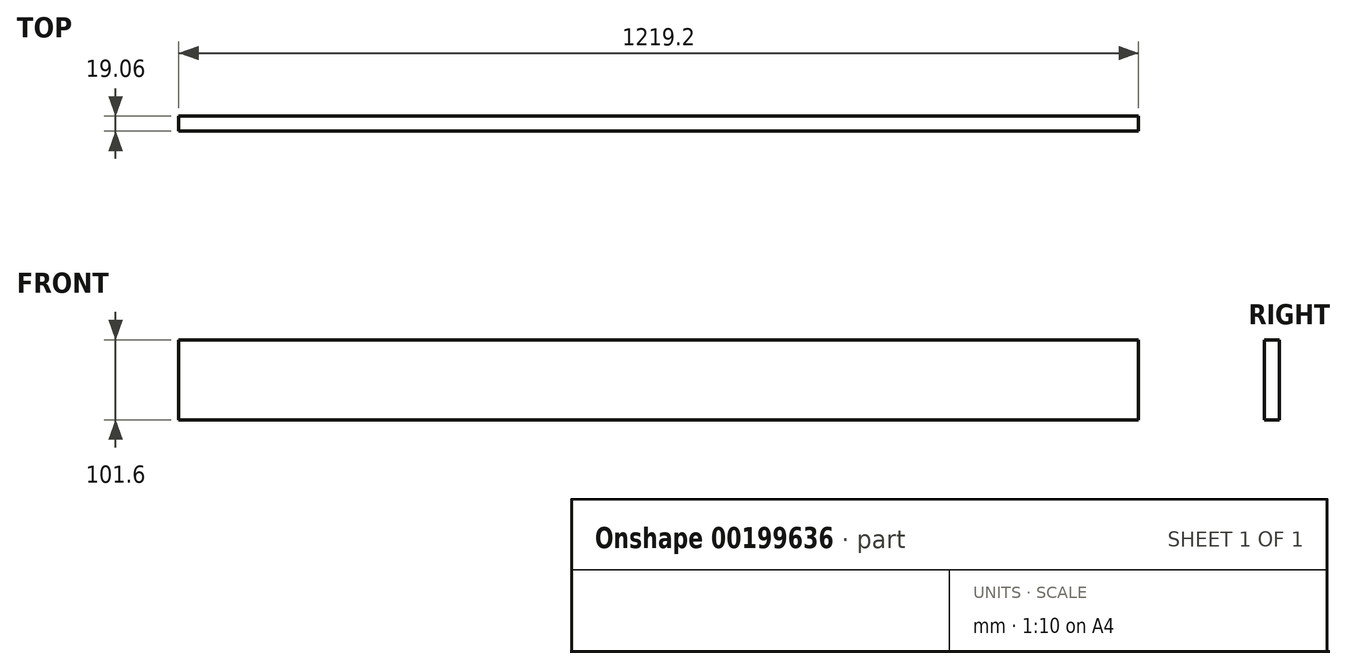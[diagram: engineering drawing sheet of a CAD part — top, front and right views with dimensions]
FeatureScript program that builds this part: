
annotation { "Feature Type Name" : "Feature", "Feature Type Description" : "" }
export const myFeature = defineFeature(function(context is Context, id is Id, definition is map)
    precondition{}
    {
        {
            var Q0;
            Q0=qCreatedBy(makeId("Front.planeOp"),FACE);
            var sketch = newSketch(context, id + "F0", { "sketchPlane" : qUnion([Q0])});
            skLineSegment(sketch, "E0.bottom", {"start": v(-557.63, 26.65) * mm, "end": v(661.57, 26.65) * mm});
            skLineSegment(sketch, "E0.top", {"start": v(-557.63, -74.95) * mm, "end": v(661.57, -74.95) * mm});
            skLineSegment(sketch, "E0.left", {"start": v(-557.63, 26.65) * mm, "end": v(-557.63, -74.95) * mm});
            skLineSegment(sketch, "E0.right", {"start": v(661.57, 26.65) * mm, "end": v(661.57, -74.95) * mm});
            skSolve(sketch);
        }
        {
            var Q0;
            Q0=makeQuery(id+"F0.imprint","IMPRINT",FACE,{"disambiguationData":[TD([[makeQuery(id+"F0.imprint","IMPRINT",EDGE,{"derivedFrom":sQuery(id+"F0.wireOp",EDGE,"E0.bottom")}),-1.0]])]});
            extrude(context, id + "F1", {"entities" : qUnion([Q0]), "endBound" : BoundingType.SYMMETRIC, "depth" : 19.05 * mm});
        }
    });
